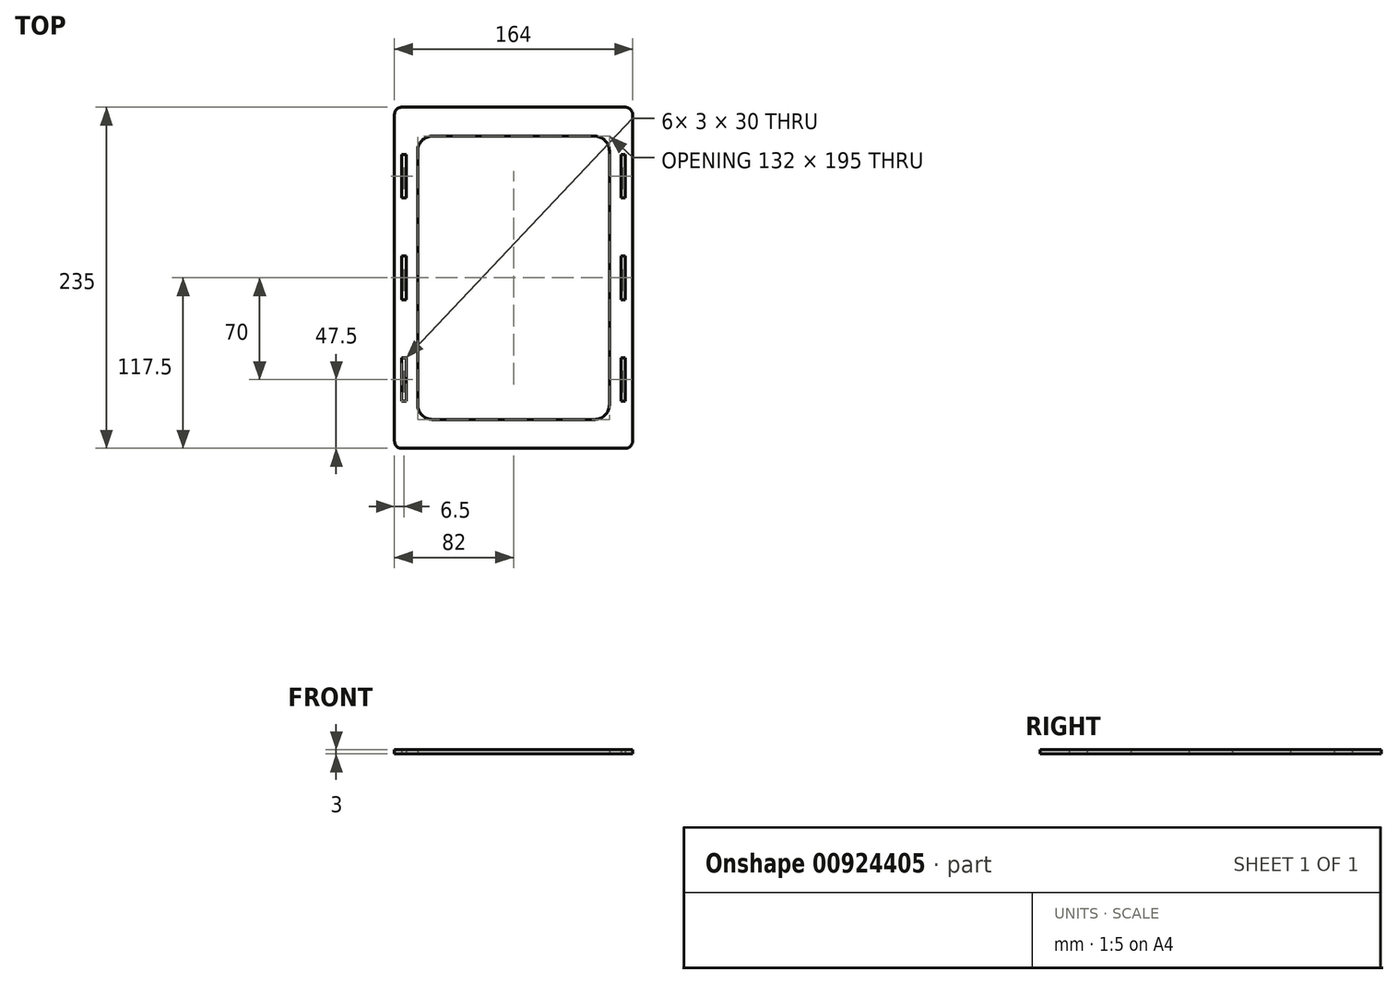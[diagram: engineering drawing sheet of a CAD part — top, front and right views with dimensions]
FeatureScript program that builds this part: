
annotation { "Feature Type Name" : "Feature", "Feature Type Description" : "" }
export const myFeature = defineFeature(function(context is Context, id is Id, definition is map)
    precondition{}
    {
        {
            var Q0;
            Q0=qCreatedBy(makeId("Top.planeOp"),FACE);
            var sketch = newSketch(context, id + "F0", { "sketchPlane" : qUnion([Q0])});
            skLineSegment(sketch, "E0.bottom", {"start": v(0, 0) * mm, "end": v(154, 0) * mm, "construction": true});
            skLineSegment(sketch, "E0.top", {"start": v(0, 225) * mm, "end": v(154, 225) * mm, "construction": true});
            skLineSegment(sketch, "E0.left", {"start": v(0, 0) * mm, "end": v(0, 225) * mm, "construction": true});
            skLineSegment(sketch, "E0.right", {"start": v(154, 0) * mm, "end": v(154, 225) * mm, "construction": true});
            skLineSegment(sketch, "E1.bottom", {"start": v(25.5, 177) * mm, "end": v(128.5, 177) * mm, "construction": true});
            skLineSegment(sketch, "E1.top", {"start": v(25.5, 120) * mm, "end": v(128.5, 120) * mm, "construction": true});
            skLineSegment(sketch, "E1.left", {"start": v(25.5, 177) * mm, "end": v(25.5, 120) * mm});
            skLineSegment(sketch, "E1.right", {"start": v(128.5, 177) * mm, "end": v(128.5, 120) * mm});
            skLineSegment(sketch, "E2", {"start": v(77, 0) * mm, "end": v(77, 225) * mm, "construction": true});
            skLineSegment(sketch, "E3", {"start": v(0, 112.5) * mm, "end": v(154, 112.5) * mm, "construction": true});
            skLineSegment(sketch, "E4.bottom", {"start": v(-5, 230) * mm, "end": v(159, 230) * mm});
            skLineSegment(sketch, "E4.top", {"start": v(-5, -5) * mm, "end": v(159, -5) * mm});
            skLineSegment(sketch, "E4.left", {"start": v(-5, 230) * mm, "end": v(-5, -5) * mm});
            skLineSegment(sketch, "E4.right", {"start": v(159, 230) * mm, "end": v(159, -5) * mm});
            skLineSegment(sketch, "E5.bottom", {"start": v(0, 127.5) * mm, "end": v(3, 127.5) * mm});
            skLineSegment(sketch, "E5.top", {"start": v(0, 97.5) * mm, "end": v(3, 97.5) * mm});
            skLineSegment(sketch, "E5.left", {"start": v(0, 127.5) * mm, "end": v(0, 97.5) * mm});
            skLineSegment(sketch, "E5.right", {"start": v(3, 127.5) * mm, "end": v(3, 97.5) * mm});
            skLineSegment(sketch, "E6.bottom", {"start": v(0, 197.5) * mm, "end": v(3, 197.5) * mm});
            skLineSegment(sketch, "E6.top", {"start": v(0, 167.5) * mm, "end": v(3, 167.5) * mm});
            skLineSegment(sketch, "E6.left", {"start": v(0, 197.5) * mm, "end": v(0, 167.5) * mm});
            skLineSegment(sketch, "E6.right", {"start": v(3, 197.5) * mm, "end": v(3, 167.5) * mm});
            skLineSegment(sketch, "E7.bottom", {"start": v(0, 57.5) * mm, "end": v(3, 57.5) * mm});
            skLineSegment(sketch, "E7.top", {"start": v(0, 27.5) * mm, "end": v(3, 27.5) * mm});
            skLineSegment(sketch, "E7.left", {"start": v(0, 57.5) * mm, "end": v(0, 27.5) * mm});
            skLineSegment(sketch, "E7.right", {"start": v(3, 57.5) * mm, "end": v(3, 27.5) * mm});
            skLineSegment(sketch, "E8.MirrorCS", {"start": v(154, 27.5) * mm, "end": v(151, 27.5) * mm});
            skLineSegment(sketch, "E9.MirrorCS", {"start": v(154, 197.5) * mm, "end": v(151, 197.5) * mm});
            skLineSegment(sketch, "E10.MirrorCS", {"start": v(154, 97.5) * mm, "end": v(151, 97.5) * mm});
            skLineSegment(sketch, "E11.MirrorCS", {"start": v(154, 57.5) * mm, "end": v(151, 57.5) * mm});
            skLineSegment(sketch, "E12.MirrorCS", {"start": v(154, 167.5) * mm, "end": v(151, 167.5) * mm});
            skLineSegment(sketch, "E13.MirrorCS", {"start": v(154, 127.5) * mm, "end": v(151, 127.5) * mm});
            skLineSegment(sketch, "E14.MirrorCS", {"start": v(154, 57.5) * mm, "end": v(154, 27.5) * mm});
            skLineSegment(sketch, "E15.MirrorCS", {"start": v(151, 197.5) * mm, "end": v(151, 167.5) * mm});
            skLineSegment(sketch, "E16.MirrorCS", {"start": v(154, 197.5) * mm, "end": v(154, 167.5) * mm});
            skLineSegment(sketch, "E17.MirrorCS", {"start": v(151, 57.5) * mm, "end": v(151, 27.5) * mm});
            skLineSegment(sketch, "E18.MirrorCS", {"start": v(151, 127.5) * mm, "end": v(151, 97.5) * mm});
            skLineSegment(sketch, "E19.MirrorCS", {"start": v(154, 127.5) * mm, "end": v(154, 97.5) * mm});
            skLineSegment(sketch, "E20.bottom", {"start": v(11, 210) * mm, "end": v(143, 210) * mm});
            skLineSegment(sketch, "E20.top", {"start": v(11, 15) * mm, "end": v(143, 15) * mm});
            skLineSegment(sketch, "E20.left", {"start": v(11, 210) * mm, "end": v(11, 15) * mm});
            skLineSegment(sketch, "E20.right", {"start": v(143, 210) * mm, "end": v(143, 15) * mm});
            skSolve(sketch);
        }
        {
            var Q0;
            Q0 = qSketchRegion(id + "F0", true);
            extrude(context, id + "F1", {"entities" : qUnion([Q0]), "depth" : 3 * mm, "offsetDistance" : 25 * mm});
        }
        {
            var Q0;
            Q0=makeQuery(id+"F1.opExtrude","SWEPT_EDGE",EDGE,{"disambiguationData":[OSD([sQuery(id+"F0.wireOp",EDGE,"E4.bottom"),sQuery(id+"F0.wireOp",EDGE,"E4.left")])]});
            var Q1;
            Q1=makeQuery(id+"F1.opExtrude","SWEPT_EDGE",EDGE,{"disambiguationData":[OSD([sQuery(id+"F0.wireOp",EDGE,"E4.bottom"),sQuery(id+"F0.wireOp",EDGE,"E4.right")])]});
            var Q2;
            Q2=makeQuery(id+"F1.opExtrude","SWEPT_EDGE",EDGE,{"disambiguationData":[OSD([sQuery(id+"F0.wireOp",EDGE,"E4.top"),sQuery(id+"F0.wireOp",EDGE,"E4.right")])]});
            var Q3;
            Q3=makeQuery(id+"F1.opExtrude","SWEPT_EDGE",EDGE,{"disambiguationData":[OSD([sQuery(id+"F0.wireOp",EDGE,"E4.top"),sQuery(id+"F0.wireOp",EDGE,"E4.left")])]});
            fillet(context, id + "F2", {"entities" : qUnion([Q0, Q1, Q2, Q3]), "radius" : 5 * mm, "tangentPropagation" : true, "allowEdgeOverflow" : false});
        }
        {
            var Q0;
            Q0=makeQuery(id+"F1.opExtrude","SWEPT_EDGE",EDGE,{"disambiguationData":[OSD([sQuery(id+"F0.wireOp",EDGE,"E20.bottom"),sQuery(id+"F0.wireOp",EDGE,"E20.left")])]});
            var Q1;
            Q1=makeQuery(id+"F1.opExtrude","SWEPT_EDGE",EDGE,{"disambiguationData":[OSD([sQuery(id+"F0.wireOp",EDGE,"E20.bottom"),sQuery(id+"F0.wireOp",EDGE,"E20.right")])]});
            var Q2;
            Q2=makeQuery(id+"F1.opExtrude","SWEPT_EDGE",EDGE,{"disambiguationData":[OSD([sQuery(id+"F0.wireOp",EDGE,"E20.top"),sQuery(id+"F0.wireOp",EDGE,"E20.right")])]});
            var Q3;
            Q3=makeQuery(id+"F1.opExtrude","SWEPT_EDGE",EDGE,{"disambiguationData":[OSD([sQuery(id+"F0.wireOp",EDGE,"E20.top"),sQuery(id+"F0.wireOp",EDGE,"E20.left")])]});
            fillet(context, id + "F3", {"entities" : qUnion([Q0, Q1, Q2, Q3]), "radius" : 10 * mm, "tangentPropagation" : true, "allowEdgeOverflow" : false});
        }
    });
